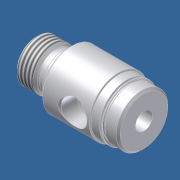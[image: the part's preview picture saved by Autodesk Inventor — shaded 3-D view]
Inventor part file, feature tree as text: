
AUTODESK INVENTOR PART (.ipt)
format: ipt  version: 2012 (Build 160160000, 160)  size: 240,128 bytes
history: native  units: in
note: dims shown in document units (in); Inventor stores cm internally (conversion verified against a paired STEP export)
features: other x106, revolve x6, sketch x6, thread x1
ambient origin geometry x8: Origin, YZ Plane, XZ Plane, XY Plane, X Axis, Y Axis, Z Axis, Center Point
bodies: Solid1 (feature_tree)
feature tree (119):
  other  "04R000_rod_guide"
  revolve  "Revolution1"  [1 undecoded]
  thread  "Thread1"  [1 undecoded]
  revolve  "Revolution2"  Angle=360.0deg
  revolve  "Revolution3"  Angle=360.0deg
  revolve  "Revolution4"  [1 undecoded]
  revolve  "Revolution5"  [1 undecoded]
  revolve  "Revolution6"  [1 undecoded]
  other  "s1_XY"
  other  "s1_YZ"
  other  "s1_ZX"
  other  "s1_X"
  other  "s1_Y"
  other  "s1_Z"
  other  "s1_Center"
  other  "s2_XY"
  other  "s2_YZ"
  other  "s2_ZX"
  other  "s2_X"
  other  "s2_Y"
  other  "s2_Z"
  other  "s2_Center"
  other  "dp1_XY"
  other  "dp1_YZ"
  other  "dp1_ZX"
  other  "dp1_X"
  other  "dp1_Y"
  other  "dp1_Z"
  other  "dp1_Center"
  other  "dp2_XY"
  other  "dp2_YZ"
  other  "dp2_ZX"
  other  "dp2_X"
  other  "dp2_Y"
  other  "dp2_Z"
  other  "dp2_Center"
  other  "rod_guide_XY"
  other  "rod_guide_YZ"
  other  "rod_guide_ZX"
  other  "rod_guide_X"
  other  "rod_guide_Y"
  other  "rod_guide_Z"
  other  "rod_guide_Center"
  other  "to_tube_XY"
  other  "to_tube_YZ"
  other  "to_tube_ZX"
  other  "to_tube_X"
  other  "to_tube_Y"
  other  "to_tube_Z"
  other  "to_tube_Center"
  other  "to_foot_bracket_XY"
  other  "to_foot_bracket_YZ"
  other  "to_foot_bracket_ZX"
  other  "to_foot_bracket_X"
  other  "to_foot_bracket_Y"
  other  "to_foot_bracket_Z"
  other  "to_foot_bracket_Center"
  other  "to_nut_XY"
  other  "to_nut_YZ"
  other  "to_nut_ZX"
  other  "to_nut_X"
  other  "to_nut_Y"
  other  "to_nut_Z"
  other  "to_nut_Center"
  other  "to_trunnion_brackets_XY"
  other  "to_trunnion_brackets_YZ"
  other  "to_trunnion_brackets_ZX"
  other  "to_trunnion_brackets_X"
  other  "to_trunnion_brackets_Y"
  other  "to_trunnion_brackets_Z"
  other  "to_trunnion_brackets_Center"
  other  "to_trunnion_brackets1_XY"
  other  "to_trunnion_brackets1_YZ"
  other  "to_trunnion_brackets1_ZX"
  other  "to_trunnion_brackets1_X"
  other  "to_trunnion_brackets1_Y"
  other  "to_trunnion_brackets1_Z"
  other  "to_trunnion_brackets1_Center"
  other  "to_trunnion_brackets2_XY"
  other  "to_trunnion_brackets2_YZ"
  other  "to_trunnion_brackets2_ZX"
  other  "to_trunnion_brackets2_X"
  other  "to_trunnion_brackets2_Y"
  other  "to_trunnion_brackets2_Z"
  other  "to_trunnion_brackets2_Center"
  other  "t111_XY"
  other  "t111_YZ"
  other  "t111_ZX"
  other  "t111_X"
  other  "t111_Y"
  other  "t111_Z"
  other  "t111_Center"
  other  "t1_XY"
  other  "t1_YZ"
  other  "t1_ZX"
  other  "t1_X"
  other  "t1_Y"
  other  "t1_Z"
  other  "t1_Center"
  other  "port_XY"
  other  "port_YZ"
  other  "port_ZX"
  other  "port_X"
  other  "port_Y"
  other  "port_Z"
  other  "port_Center"
  other  "to_screw_XY"
  other  "to_screw_YZ"
  other  "to_screw_ZX"
  other  "to_screw_X"
  other  "to_screw_Y"
  other  "to_screw_Z"
  other  "to_screw_Center"
  sketch  "Sketch_2"  dims[d0=360.0deg d1=0.2961in d2=0.0in d3=360.0deg]
  sketch  "Sketch_3"  dims[d4=360.0deg d5=360.0deg]
  sketch  "Sketch_5"  dims[d6=360.0deg d7=360.0deg]
  sketch  "Sketch_10"
  sketch  "Sketch_40"
  sketch  "Sketch_47"
note: 5 required parameter values undecoded (feature->parameter linkage not recoverable at this tier; creation-order binding heuristic only, values carry confidence <= 0.55)